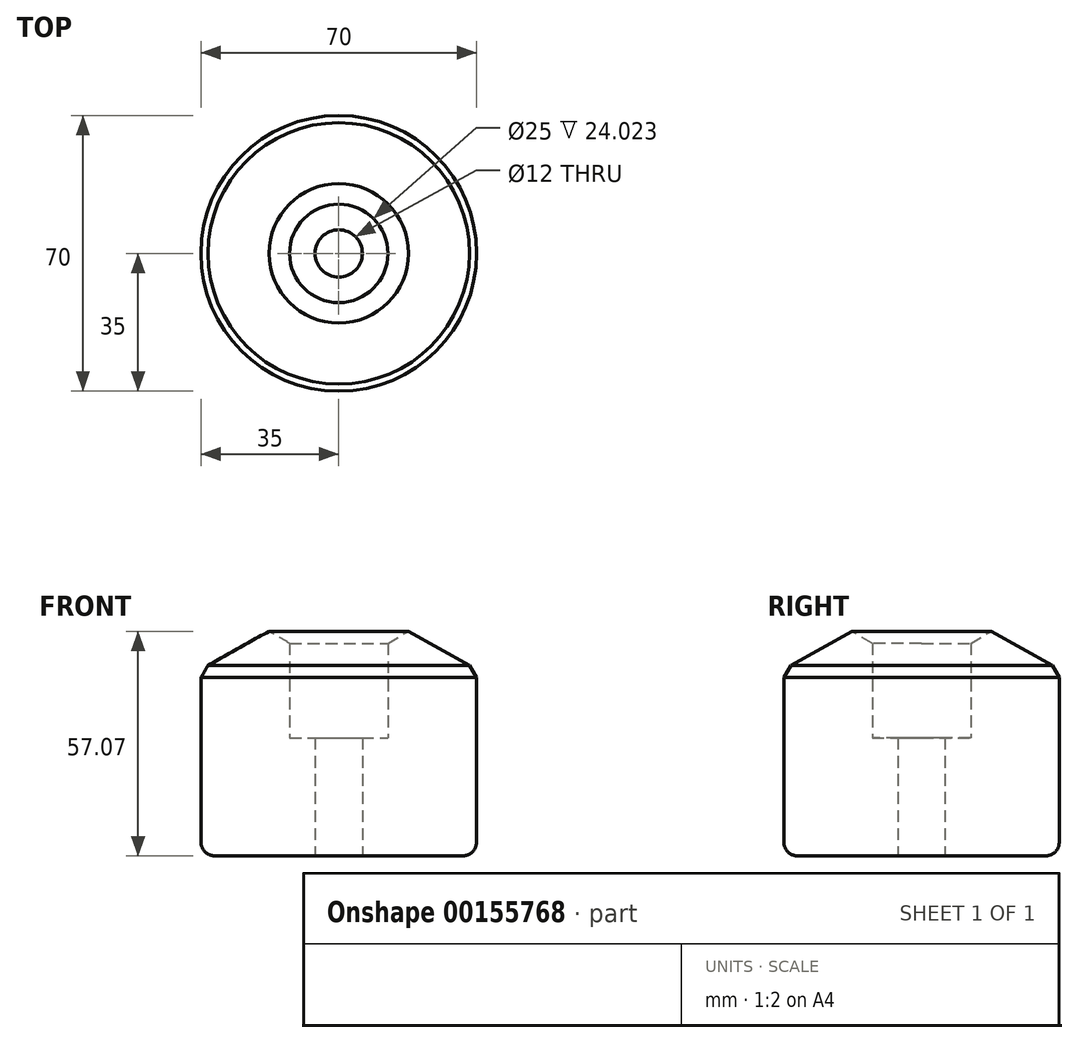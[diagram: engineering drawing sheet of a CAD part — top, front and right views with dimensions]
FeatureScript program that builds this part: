
annotation { "Feature Type Name" : "Feature", "Feature Type Description" : "" }
export const myFeature = defineFeature(function(context is Context, id is Id, definition is map)
    precondition{}
    {
        {
            var Q0;
            Q0=qCreatedBy(makeId("Front.planeOp"),FACE);
            var sketch = newSketch(context, id + "F0", { "sketchPlane" : qUnion([Q0])});
            skLineSegment(sketch, "E0", {"start": v(35, -30.44) * mm, "end": v(35, 16.93) * mm});
            skLineSegment(sketch, "E1", {"start": v(35, 16.93) * mm, "end": v(12.5, 29.56) * mm});
            skLineSegment(sketch, "E2", {"start": v(0, 0) * mm, "end": v(0, 43.74) * mm, "construction": true});
            skLineSegment(sketch, "E3", {"start": v(6, -0.44) * mm, "end": v(12.5, -0.44) * mm});
            skLineSegment(sketch, "E4", {"start": v(12.5, -0.44) * mm, "end": v(12.5, 29.56) * mm});
            skPoint(sketch, "E5.orphan", {"position": v(6, 33.2) * mm});
            skLineSegment(sketch, "E6", {"start": v(6, -0.44) * mm, "end": v(6, -30.44) * mm});
            skLineSegment(sketch, "E7", {"start": v(6, -30.44) * mm, "end": v(35, -30.44) * mm});
            skSolve(sketch);
        }
        {
            var Q0;
            Q0=makeQuery(id+"F0.imprint","IMPRINT",FACE,{"disambiguationData":[TD([[makeQuery(id+"F0.imprint","IMPRINT",EDGE,{"derivedFrom":sQuery(id+"F0.wireOp",EDGE,"E0")}),1.0]])]});
            var Q1;
            Q1=sQuery(id+"F0.wireOp",EDGE,"E2");
            revolve(context, id + "F1", {"entities" : qUnion([Q0]), "axis" : qUnion([Q1]), "revolveType" : RevolveType.FULL});
        }
        {
            var Q0;
            Q0=makeQuery(id+"F1.opRevolve","SWEPT_EDGE",EDGE,{"disambiguationData":[OSD([sQuery(id+"F0.wireOp",EDGE,"E0"),sQuery(id+"F0.wireOp",EDGE,"E1")])]});
            var Q1;
            Q1=makeQuery(id+"F1.opRevolve","SWEPT_EDGE",EDGE,{"disambiguationData":[OSD([sQuery(id+"F0.wireOp",EDGE,"E1"),sQuery(id+"F0.wireOp",EDGE,"E4")])]});
            chamfer(context, id + "F2", {"entities" : qUnion([Q0, Q1]), "width" : 3.5 * mm, "tangentPropagation" : true});
        }
        {
            var Q0;
            Q0=makeQuery(id+"F1.opRevolve","SWEPT_EDGE",EDGE,{"disambiguationData":[OSD([sQuery(id+"F0.wireOp",EDGE,"E0"),sQuery(id+"F0.wireOp",EDGE,"E7")])]});
            fillet(context, id + "F3", {"entities" : qUnion([Q0]), "radius" : 3.5 * mm, "tangentPropagation" : true, "allowEdgeOverflow" : false});
        }
    });
